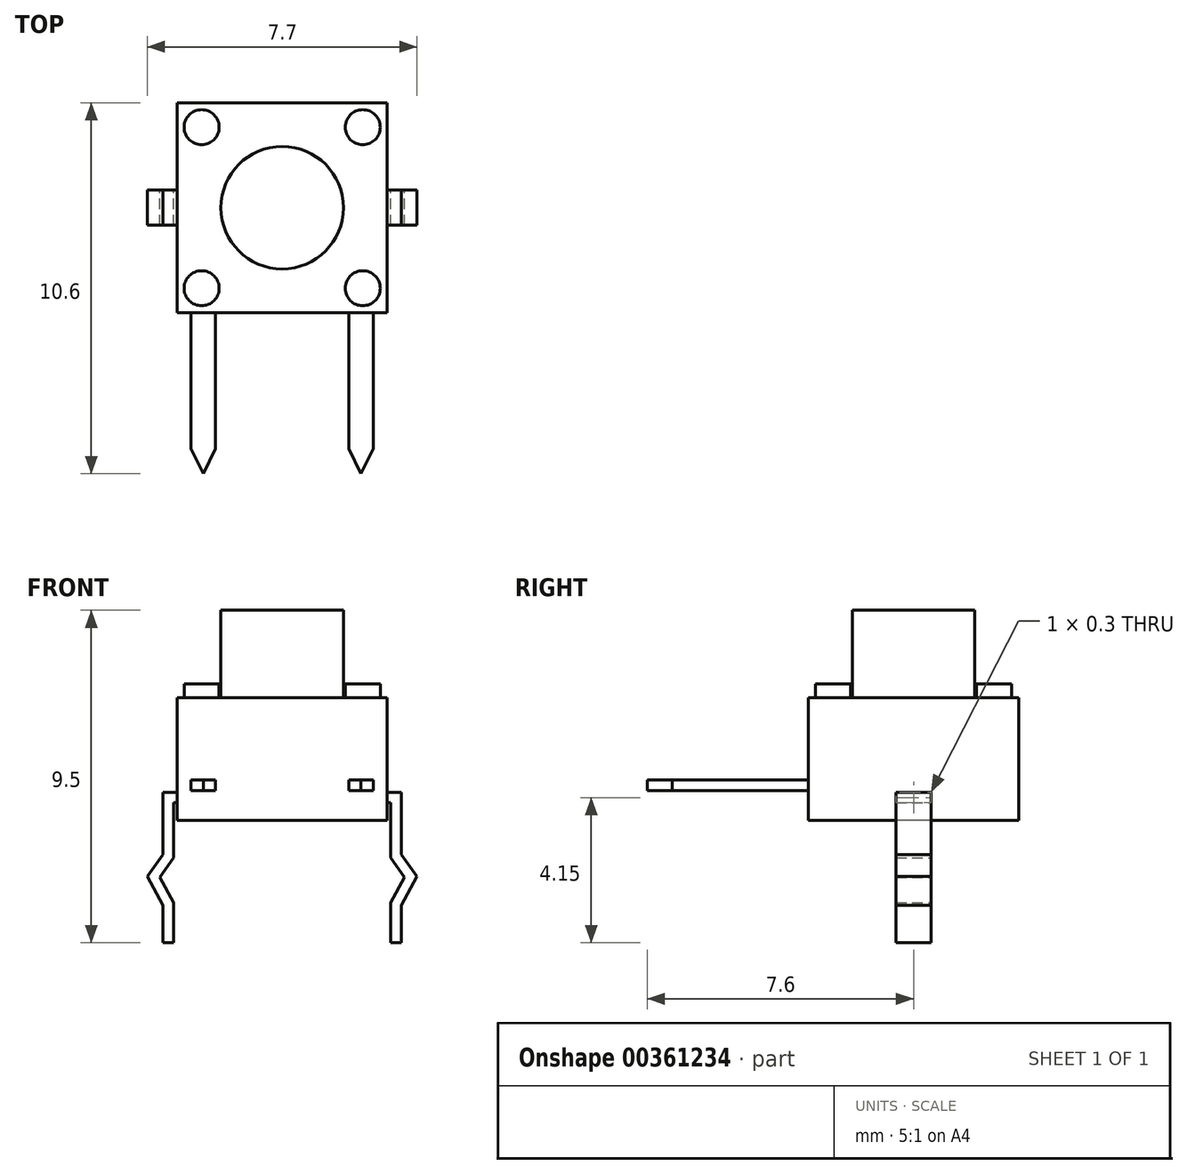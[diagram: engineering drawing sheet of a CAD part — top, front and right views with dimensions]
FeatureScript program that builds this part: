
annotation { "Feature Type Name" : "Feature", "Feature Type Description" : "" }
export const myFeature = defineFeature(function(context is Context, id is Id, definition is map)
    precondition{}
    {
        {
            var Q0;
            Q0=qCreatedBy(makeId("Top.planeOp"),FACE);
            var sketch = newSketch(context, id + "F0", { "sketchPlane" : qUnion([Q0])});
            skLineSegment(sketch, "E0.bottom", {"start": v(3, 1.75) * mm, "end": v(-3, 1.75) * mm});
            skLineSegment(sketch, "E0.top", {"start": v(3, -1.75) * mm, "end": v(-3, -1.75) * mm});
            skLineSegment(sketch, "E0.left", {"start": v(3, 1.75) * mm, "end": v(3, -1.75) * mm});
            skLineSegment(sketch, "E0.right", {"start": v(-3, 1.75) * mm, "end": v(-3, -1.75) * mm});
            skPoint(sketch, "E0.middle", {"position": v(0, 0) * mm});
            skSolve(sketch);
        }
        {
            var Q0;
            Q0=qSketchRegion(id+"F0",true);
            extrude(context, id + "F1", {"entities" : qUnion([Q0]), "depth" : 3.3 * mm, "offsetDistance" : 25 * mm});
        }
        {
            var Q0;
            Q0=makeQuery(id+"F1.opExtrude","CAP_FACE",FACE,{"disambiguationData":[OSD([sQuery(id+"F0.wireOp",EDGE,"E0.bottom"),sQuery(id+"F0.wireOp",EDGE,"E0.top"),sQuery(id+"F0.wireOp",EDGE,"E0.left"),sQuery(id+"F0.wireOp",EDGE,"E0.right")])],"isStart":false});
            var sketch = newSketch(context, id + "F2", { "sketchPlane" : qUnion([Q0])});
            skLineSegment(sketch, "E1.bottom", {"start": v(-1.47, 0.72) * mm, "end": v(1.48, 0.72) * mm});
            skLineSegment(sketch, "E1.top", {"start": v(-1.48, -0.72) * mm, "end": v(1.47, -0.72) * mm});
            skLineSegment(sketch, "E1.left", {"start": v(-1.47, 0.72) * mm, "end": v(-1.48, -0.72) * mm});
            skLineSegment(sketch, "E1.right", {"start": v(1.48, 0.72) * mm, "end": v(1.47, -0.72) * mm});
            skPoint(sketch, "E1.middle", {"position": v(0, 0) * mm});
            skSolve(sketch);
        }
        {
            var Q0;
            Q0=qSketchRegion(id+"F2",true);
            extrude(context, id + "F3", {"entities" : qUnion([Q0]), "operationType" : NewBodyOperationType.ADD, "depth" : 1 * mm, "offsetDistance" : 25 * mm});
        }
        {
            var Q0;
            Q0=qCreatedBy(makeId("Front.planeOp"),FACE);
            var sketch = newSketch(context, id + "F4", { "sketchPlane" : qUnion([Q0])});
            skLineSegment(sketch, "E2", {"start": v(-2.86, 0.8) * mm, "end": v(-3.4, 0.8) * mm});
            skLineSegment(sketch, "E3", {"start": v(-3.4, 0.8) * mm, "end": v(-3.4, -0.98) * mm});
            skLineSegment(sketch, "E4", {"start": v(-3.4, -0.98) * mm, "end": v(-3.85, -1.6) * mm});
            skLineSegment(sketch, "E5", {"start": v(-3.85, -1.6) * mm, "end": v(-3.4, -2.43) * mm});
            skLineSegment(sketch, "E6", {"start": v(-3.4, -2.43) * mm, "end": v(-3.4, -3.5) * mm});
            skLineSegment(sketch, "E7", {"start": v(-3.4, -3.5) * mm, "end": v(-3.1, -3.5) * mm});
            skPoint(sketch, "E8", {"position": v(-3.25, -3.5) * mm});
            skLineSegment(sketch, "E9.0", {"start": v(-3.1, -2.35) * mm, "end": v(-3.1, -3.5) * mm});
            skLineSegment(sketch, "E9.1", {"start": v(-3.5, -1.62) * mm, "end": v(-3.1, -2.35) * mm});
            skLineSegment(sketch, "E9.2", {"start": v(-3.1, -1.07) * mm, "end": v(-3.5, -1.62) * mm});
            skLineSegment(sketch, "E9.3", {"start": v(-3.1, 0.5) * mm, "end": v(-3.1, -1.07) * mm});
            skLineSegment(sketch, "E10", {"start": v(-3.1, 0.5) * mm, "end": v(-2.86, 0.5) * mm});
            skLineSegment(sketch, "E11", {"start": v(-2.86, 0.5) * mm, "end": v(-2.86, 0.8) * mm});
            skLineSegment(sketch, "E12", {"start": v(0, -0.55) * mm, "end": v(0, -1.95) * mm, "construction": true});
            skLineSegment(sketch, "E13.MirrorCS", {"start": v(2.86, 0.5) * mm, "end": v(2.86, 0.8) * mm});
            skLineSegment(sketch, "E14.MirrorCS", {"start": v(3.1, 0.5) * mm, "end": v(2.86, 0.5) * mm});
            skLineSegment(sketch, "E15.MirrorCS", {"start": v(3.4, -3.5) * mm, "end": v(3.1, -3.5) * mm});
            skLineSegment(sketch, "E16.MirrorCS", {"start": v(3.1, -2.35) * mm, "end": v(3.1, -3.5) * mm});
            skPoint(sketch, "E17.MirrorP", {"position": v(3.25, -3.5) * mm});
            skLineSegment(sketch, "E18.MirrorCS", {"start": v(3.5, -1.62) * mm, "end": v(3.1, -2.35) * mm});
            skLineSegment(sketch, "E19.MirrorCS", {"start": v(3.1, -1.07) * mm, "end": v(3.5, -1.62) * mm});
            skLineSegment(sketch, "E20.MirrorCS", {"start": v(3.85, -1.6) * mm, "end": v(3.4, -2.43) * mm});
            skLineSegment(sketch, "E21.MirrorCS", {"start": v(3.4, -2.43) * mm, "end": v(3.4, -3.5) * mm});
            skLineSegment(sketch, "E22.MirrorCS", {"start": v(3.4, 0.8) * mm, "end": v(3.4, -0.98) * mm});
            skLineSegment(sketch, "E23.MirrorCS", {"start": v(2.86, 0.8) * mm, "end": v(3.4, 0.8) * mm});
            skLineSegment(sketch, "E24.MirrorCS", {"start": v(3.4, -0.98) * mm, "end": v(3.85, -1.6) * mm});
            skLineSegment(sketch, "E25.MirrorCS", {"start": v(3.1, 0.5) * mm, "end": v(3.1, -1.07) * mm});
            skSolve(sketch);
        }
        {
            var Q0;
            Q0=qSketchRegion(id+"F4",true);
            extrude(context, id + "F5", {"entities" : qUnion([Q0]), "operationType" : NewBodyOperationType.ADD, "depth" : 1 * mm, "offsetDistance" : 25 * mm, "symmetric" : true});
        }
        {
            var Q0;
            Q0=makeQuery(id+"F3.opExtrude","CAP_FACE",FACE,{"disambiguationData":[OSD([sQuery(id+"F2.wireOp",EDGE,"E1.bottom"),sQuery(id+"F2.wireOp",EDGE,"E1.top"),sQuery(id+"F2.wireOp",EDGE,"E1.left"),sQuery(id+"F2.wireOp",EDGE,"E1.right")])],"isStart":false});
            var Q1;
            Q1=makeQuery(id+"F3.opExtrude","SWEPT_EDGE",EDGE,{"disambiguationData":[OSD([sQuery(id+"F2.wireOp",EDGE,"E1.top"),sQuery(id+"F2.wireOp",EDGE,"E1.left")])]});
            var Q2;
            Q2=makeQuery(id+"F3.opExtrude","SWEPT_EDGE",EDGE,{"disambiguationData":[OSD([sQuery(id+"F2.wireOp",EDGE,"E1.top"),sQuery(id+"F2.wireOp",EDGE,"E1.right")])]});
            var Q3;
            Q3=makeQuery(id+"F3.opExtrude","SWEPT_EDGE",EDGE,{"disambiguationData":[OSD([sQuery(id+"F2.wireOp",EDGE,"E1.bottom"),sQuery(id+"F2.wireOp",EDGE,"E1.right")])]});
            var Q4;
            Q4=makeQuery(id+"F3.opExtrude","SWEPT_EDGE",EDGE,{"disambiguationData":[OSD([sQuery(id+"F2.wireOp",EDGE,"E1.bottom"),sQuery(id+"F2.wireOp",EDGE,"E1.left")])]});
            fillet(context, id + "F6", {"entities" : qUnion([Q0, Q1, Q2, Q3, Q4]), "radius" : 0.2 * mm, "tangentPropagation" : true, "allowEdgeOverflow" : false});
        }
        {
            var Q0;
            Q0=qCreatedBy(makeId("Top.planeOp"),FACE);
            var sketch = newSketch(context, id + "F7", { "sketchPlane" : qUnion([Q0])});
            skLineSegment(sketch, "E26.bottom", {"start": v(3, 3) * mm, "end": v(-3, 3) * mm});
            skLineSegment(sketch, "E26.top", {"start": v(3, -3) * mm, "end": v(-3, -3) * mm});
            skLineSegment(sketch, "E26.left", {"start": v(3, 3) * mm, "end": v(3, -3) * mm});
            skLineSegment(sketch, "E26.right", {"start": v(-3, 3) * mm, "end": v(-3, -3) * mm});
            skPoint(sketch, "E26.middle", {"position": v(0, 0) * mm});
            skSolve(sketch);
        }
        {
            var Q0;
            Q0=qSketchRegion(id+"F7",true);
            extrude(context, id + "F8", {"entities" : qUnion([Q0]), "depth" : 3.5 * mm, "offsetDistance" : 25 * mm});
        }
        {
            var Q0;
            Q0=makeQuery(id+"F8.opExtrude","CAP_FACE",FACE,{"disambiguationData":[OSD([sQuery(id+"F7.wireOp",EDGE,"E26.bottom"),sQuery(id+"F7.wireOp",EDGE,"E26.top"),sQuery(id+"F7.wireOp",EDGE,"E26.left"),sQuery(id+"F7.wireOp",EDGE,"E26.right")])],"isStart":false});
            var sketch = newSketch(context, id + "F9", { "sketchPlane" : qUnion([Q0])});
            skCircle(sketch, "E27", {"center": v(0, 0) * mm, "radius": 1.75 * mm});
            skSolve(sketch);
        }
        {
            var Q0;
            Q0=qSketchRegion(id+"F9",true);
            extrude(context, id + "F10", {"entities" : qUnion([Q0]), "operationType" : NewBodyOperationType.ADD, "depth" : (6 - 3.5) * mm, "offsetDistance" : 25 * mm});
        }
        {
            var Q0;
            Q0=makeQuery(id+"F8.opExtrude","CAP_FACE",FACE,{"disambiguationData":[OSD([sQuery(id+"F7.wireOp",EDGE,"E26.bottom"),sQuery(id+"F7.wireOp",EDGE,"E26.top"),sQuery(id+"F7.wireOp",EDGE,"E26.left"),sQuery(id+"F7.wireOp",EDGE,"E26.right")])],"isStart":false});
            var sketch = newSketch(context, id + "F11", { "sketchPlane" : qUnion([Q0])});
            skCircle(sketch, "E28", {"center": v(-2.3, 2.3) * mm, "radius": 0.5 * mm});
            skCircle(sketch, "E29.0.1.0", {"center": v(-2.3, -2.3) * mm, "radius": 0.5 * mm});
            skCircle(sketch, "E29.1.0.0", {"center": v(2.3, 2.3) * mm, "radius": 0.5 * mm});
            skCircle(sketch, "E29.1.1.0", {"center": v(2.3, -2.3) * mm, "radius": 0.5 * mm});
            skLineSegment(sketch, "E29.direction1", {"start": v(-2.3, 2.3) * mm, "end": v(2.3, 2.3) * mm, "construction": true});
            skLineSegment(sketch, "E29.direction2", {"start": v(-2.3, 2.3) * mm, "end": v(-2.3, -2.3) * mm, "construction": true});
            skSolve(sketch);
        }
        {
            var Q0;
            Q0=qSketchRegion(id+"F11",true);
            extrude(context, id + "F12", {"entities" : qUnion([Q0]), "operationType" : NewBodyOperationType.ADD, "depth" : 0.4 * mm, "offsetDistance" : 25 * mm});
        }
        {
            var Q0;
            Q0=qCreatedBy(makeId("Top.planeOp"),FACE);
            cPlane(context, id + "F13", {"entities" : qUnion([Q0]), "cplaneType" : CPlaneType.OFFSET, "offset" : 1 * mm, "width" : 150 * mm, "height" : 150 * mm});
        }
        {
            var Q0;
            Q0=qCreatedBy(id+"F13.planeOp",FACE);
            var sketch = newSketch(context, id + "F14", { "sketchPlane" : qUnion([Q0])});
            skLineSegment(sketch, "E30", {"start": v(-2.6, -3) * mm, "end": v(-2.6, -6.89) * mm});
            skLineSegment(sketch, "E31", {"start": v(-2.6, -6.89) * mm, "end": v(-2.25, -7.6) * mm});
            skLineSegment(sketch, "E32", {"start": v(-2.25, -7.6) * mm, "end": v(-1.9, -6.89) * mm});
            skLineSegment(sketch, "E33", {"start": v(-1.9, -6.89) * mm, "end": v(-1.9, -3) * mm});
            skLineSegment(sketch, "E34", {"start": v(-1.9, -3) * mm, "end": v(-2.6, -3) * mm});
            skLineSegment(sketch, "E35", {"start": v(0, -0.67) * mm, "end": v(0, -4.64) * mm});
            skLineSegment(sketch, "E36", {"start": v(-2.25, -7.6) * mm, "end": v(-2.25, -5.07) * mm, "construction": true});
            skLineSegment(sketch, "E37.MirrorCS", {"start": v(-2.25, -7.6) * mm, "end": v(-2.6, -6.89) * mm});
            skLineSegment(sketch, "E38.MirrorCS", {"start": v(-2.6, -6.89) * mm, "end": v(-2.6, -3) * mm});
            skLineSegment(sketch, "E39.MirrorCS", {"start": v(-1.9, -3) * mm, "end": v(-1.9, -6.89) * mm});
            skLineSegment(sketch, "E40.MirrorCS", {"start": v(-2.6, -3) * mm, "end": v(-1.9, -3) * mm});
            skLineSegment(sketch, "E41.MirrorCS", {"start": v(-1.9, -6.89) * mm, "end": v(-2.25, -7.6) * mm});
            skLineSegment(sketch, "E42.MirrorCS", {"start": v(2.6, -3) * mm, "end": v(1.9, -3) * mm});
            skLineSegment(sketch, "E43.MirrorCS", {"start": v(2.25, -7.6) * mm, "end": v(2.6, -6.89) * mm});
            skLineSegment(sketch, "E44.MirrorCS", {"start": v(1.9, -6.89) * mm, "end": v(1.9, -3) * mm});
            skLineSegment(sketch, "E45.MirrorCS", {"start": v(2.25, -7.6) * mm, "end": v(1.9, -6.89) * mm});
            skLineSegment(sketch, "E46.MirrorCS", {"start": v(2.6, -6.89) * mm, "end": v(2.6, -3) * mm});
            skLineSegment(sketch, "E47.MirrorCS", {"start": v(1.9, -6.89) * mm, "end": v(2.25, -7.6) * mm});
            skLineSegment(sketch, "E48.MirrorCS", {"start": v(2.6, -6.89) * mm, "end": v(2.25, -7.6) * mm});
            skLineSegment(sketch, "E49.MirrorCS", {"start": v(2.6, -3) * mm, "end": v(2.6, -6.89) * mm});
            skLineSegment(sketch, "E50.MirrorCS", {"start": v(1.9, -3) * mm, "end": v(1.9, -6.89) * mm});
            skLineSegment(sketch, "E51.MirrorCS", {"start": v(1.9, -3) * mm, "end": v(2.6, -3) * mm});
            skSolve(sketch);
        }
        {
            var Q0;
            Q0=qSketchRegion(id+"F14",true);
            extrude(context, id + "F15", {"entities" : qUnion([Q0]), "operationType" : NewBodyOperationType.ADD, "depth" : 0.3 * mm, "offsetDistance" : 25 * mm, "symmetric" : true});
        }
    });
